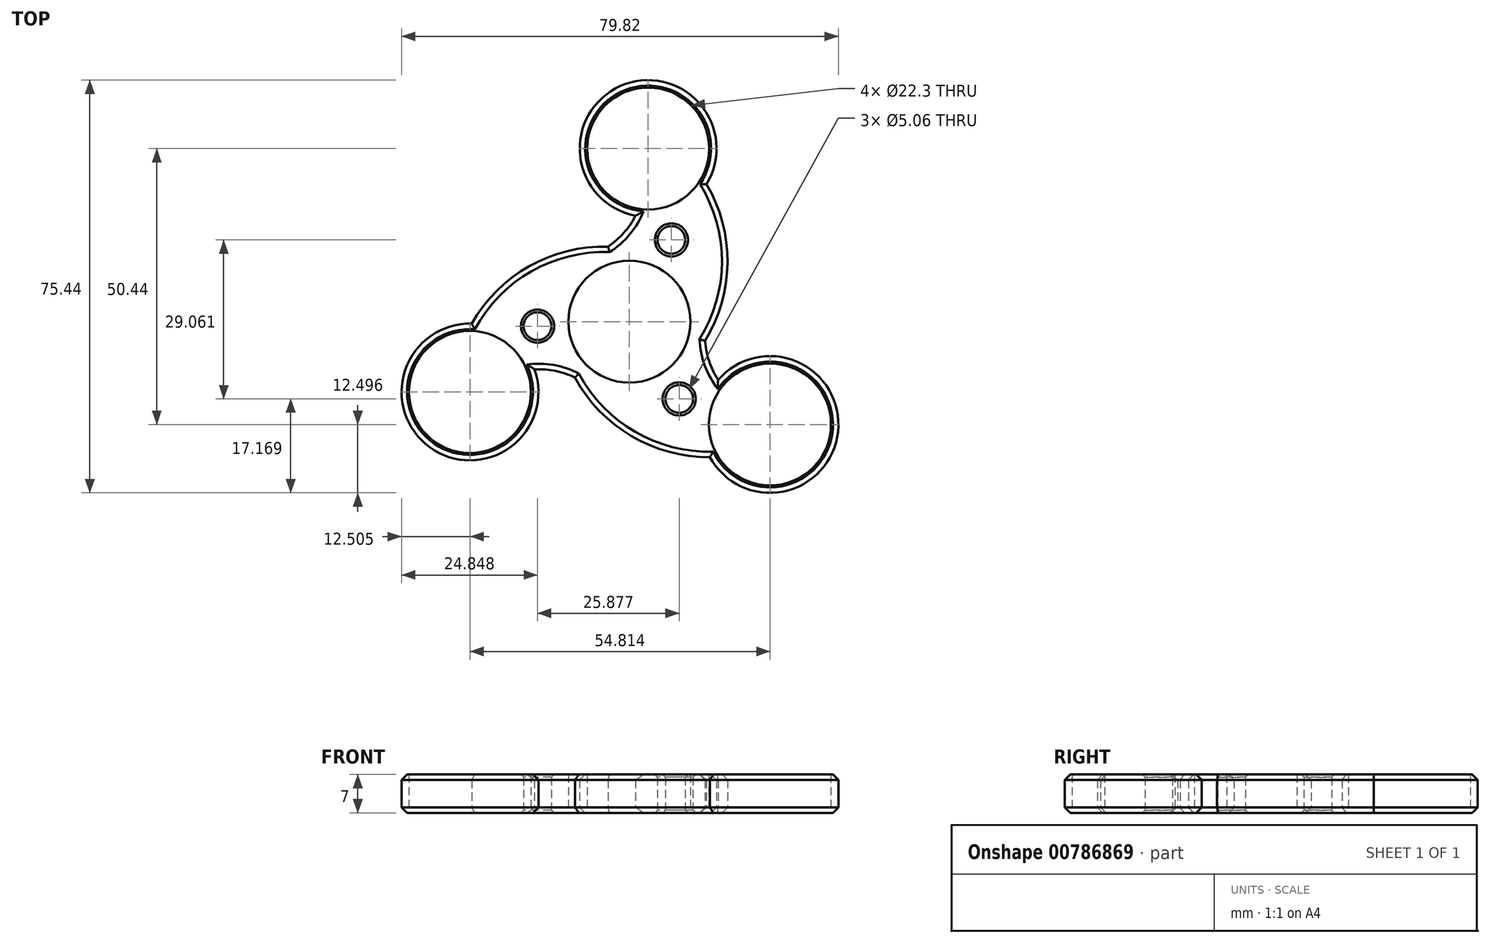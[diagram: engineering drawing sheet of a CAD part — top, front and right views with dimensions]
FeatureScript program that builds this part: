
annotation { "Feature Type Name" : "Feature", "Feature Type Description" : "" }
export const myFeature = defineFeature(function(context is Context, id is Id, definition is map)
    precondition{}
    {
        {
            var Q0;
            Q0=qCreatedBy(makeId("Top.planeOp"),FACE);
            var sketch = newSketch(context, id + "F0", { "sketchPlane" : qUnion([Q0])});
            skCircle(sketch, "E0", {"center": v(-20.85, 25.1) * mm, "radius": 11.15 * mm});
            skArc(sketch, "E1", {"start": v(-30.79, 14.88) * mm, "mid": v(-20.48, 4.2) * mm, "end": v(-6.14, 0.34) * mm});
            skArc(sketch, "E2", {"start": v(-7.03, 21.62) * mm, "mid": v(-6.3, 17.89) * mm, "end": v(-4.64, 14.46) * mm});
            skCircle(sketch, "E3", {"center": v(4.84, 6.32) * mm, "radius": 11.15 * mm});
            skArc(sketch, "E4", {"start": v(-6.14, 0.34) * mm, "mid": v(17.27, 5) * mm, "end": v(-4.64, 14.46) * mm});
            skArc(sketch, "E5.1.0", {"start": v(-24.74, 38.83) * mm, "mid": v(-21.88, 41.33) * mm, "end": v(-19.74, 44.47) * mm});
            skCircle(sketch, "E5.1.1", {"center": v(-17.42, 56.76) * mm, "radius": 11.15 * mm});
            skArc(sketch, "E5.1.2", {"start": v(-6.76, 50.24) * mm, "mid": v(-22.5, 68.18) * mm, "end": v(-19.74, 44.47) * mm});
            skArc(sketch, "E5.1.3", {"start": v(-7.03, 21.62) * mm, "mid": v(-2.94, 35.9) * mm, "end": v(-6.76, 50.24) * mm});
            skArc(sketch, "E5.2.0", {"start": v(-30.79, 14.88) * mm, "mid": v(-34.39, 16.11) * mm, "end": v(-38.18, 16.4) * mm});
            skCircle(sketch, "E5.2.1", {"center": v(-49.98, 12.26) * mm, "radius": 11.15 * mm});
            skArc(sketch, "E5.2.2", {"start": v(-49.66, 24.75) * mm, "mid": v(-57.33, 2.15) * mm, "end": v(-38.18, 16.4) * mm});
            skArc(sketch, "E5.2.3", {"start": v(-24.74, 38.83) * mm, "mid": v(-39.15, 35.24) * mm, "end": v(-49.66, 24.75) * mm});
            skPoint(sketch, "E6.trimOffspring.end.orphan", {"position": v(-6.85, 25.1) * mm});
            skPoint(sketch, "E7.orphan", {"position": v(-7.52, 20.85) * mm});
            skPoint(sketch, "E8.orphan", {"position": v(-27.85, 12.99) * mm});
            skPoint(sketch, "E9.orphan", {"position": v(-31.21, 15.7) * mm});
            skPoint(sketch, "E10.orphan", {"position": v(-27.85, 37.23) * mm});
            skPoint(sketch, "E11.orphan", {"position": v(-23.83, 38.79) * mm});
            skCircle(sketch, "E12", {"center": v(-13.17, 40.05) * mm, "radius": 2.53 * mm});
            skCircle(sketch, "E13.1.0", {"center": v(-37.63, 24.3) * mm, "radius": 2.53 * mm});
            skCircle(sketch, "E13.2.0", {"center": v(-11.75, 10.99) * mm, "radius": 2.53 * mm});
            skSolve(sketch);
        }
        {
            var Q0;
            Q0=qSketchRegion(id+"F0",true);
            extrude(context, id + "F1", {"entities" : qUnion([Q0]), "depth" : 7 * mm, "offsetDistance" : 25 * mm});
        }
        {
            var Q0;
            Q0=makeQuery(id+"F1.opExtrude","CAP_EDGE",EDGE,{"disambiguationData":[OSD([sQuery(id+"F0.wireOp",EDGE,"E5.2.3")])],"isStart":true});
            var Q1;
            Q1=makeQuery(id+"F1.opExtrude","CAP_EDGE",EDGE,{"disambiguationData":[OSD([sQuery(id+"F0.wireOp",EDGE,"E5.2.3")])],"isStart":false});
            var Q2;
            Q2=makeQuery(id+"F1.opExtrude","CAP_EDGE",EDGE,{"disambiguationData":[OSD([sQuery(id+"F0.wireOp",EDGE,"E5.2.2")])],"isStart":true});
            var Q3;
            Q3=makeQuery(id+"F1.opExtrude","CAP_EDGE",EDGE,{"disambiguationData":[OSD([sQuery(id+"F0.wireOp",EDGE,"E5.2.2")])],"isStart":false});
            var Q4;
            Q4=makeQuery(id+"F1.opExtrude","CAP_EDGE",EDGE,{"disambiguationData":[OSD([sQuery(id+"F0.wireOp",EDGE,"E5.1.0")])],"isStart":false});
            var Q5;
            Q5=makeQuery(id+"F1.opExtrude","CAP_EDGE",EDGE,{"disambiguationData":[OSD([sQuery(id+"F0.wireOp",EDGE,"E5.1.0")])],"isStart":true});
            var Q6;
            Q6=makeQuery(id+"F1.opExtrude","CAP_EDGE",EDGE,{"disambiguationData":[OSD([sQuery(id+"F0.wireOp",EDGE,"E5.1.2")])],"isStart":true});
            var Q7;
            Q7=makeQuery(id+"F1.opExtrude","CAP_EDGE",EDGE,{"disambiguationData":[OSD([sQuery(id+"F0.wireOp",EDGE,"E5.1.2")])],"isStart":false});
            var Q8;
            Q8=makeQuery(id+"F1.opExtrude","CAP_EDGE",EDGE,{"disambiguationData":[OSD([sQuery(id+"F0.wireOp",EDGE,"E5.1.3")])],"isStart":true});
            var Q9;
            Q9=makeQuery(id+"F1.opExtrude","CAP_EDGE",EDGE,{"disambiguationData":[OSD([sQuery(id+"F0.wireOp",EDGE,"E5.1.3")])],"isStart":false});
            var Q10;
            Q10=makeQuery(id+"F1.opExtrude","CAP_EDGE",EDGE,{"disambiguationData":[OSD([sQuery(id+"F0.wireOp",EDGE,"E2")])],"isStart":false});
            var Q11;
            Q11=makeQuery(id+"F1.opExtrude","CAP_EDGE",EDGE,{"disambiguationData":[OSD([sQuery(id+"F0.wireOp",EDGE,"E2")])],"isStart":true});
            var Q12;
            Q12=makeQuery(id+"F1.opExtrude","CAP_EDGE",EDGE,{"disambiguationData":[OSD([sQuery(id+"F0.wireOp",EDGE,"E4")])],"isStart":true});
            var Q13;
            Q13=makeQuery(id+"F1.opExtrude","CAP_EDGE",EDGE,{"disambiguationData":[OSD([sQuery(id+"F0.wireOp",EDGE,"E4")])],"isStart":false});
            var Q14;
            Q14=makeQuery(id+"F1.opExtrude","CAP_EDGE",EDGE,{"disambiguationData":[OSD([sQuery(id+"F0.wireOp",EDGE,"E1")])],"isStart":true});
            var Q15;
            Q15=makeQuery(id+"F1.opExtrude","CAP_EDGE",EDGE,{"disambiguationData":[OSD([sQuery(id+"F0.wireOp",EDGE,"E1")])],"isStart":false});
            var Q16;
            Q16=makeQuery(id+"F1.opExtrude","CAP_EDGE",EDGE,{"disambiguationData":[OSD([sQuery(id+"F0.wireOp",EDGE,"E5.2.0")])],"isStart":false});
            var Q17;
            Q17=makeQuery(id+"F1.opExtrude","CAP_EDGE",EDGE,{"disambiguationData":[OSD([sQuery(id+"F0.wireOp",EDGE,"E5.2.0")])],"isStart":true});
            chamfer(context, id + "F2", {"entities" : qUnion([Q0, Q1, Q2, Q3, Q4, Q5, Q6, Q7, Q8, Q9, Q10, Q11, Q12, Q13, Q14, Q15, Q16, Q17]), "width" : 1 * mm, "tangentPropagation" : true});
        }
        {
            var Q0;
            Q0=makeQuery(id+"F1.opExtrude","CAP_EDGE",EDGE,{"disambiguationData":[OSD([sQuery(id+"F0.wireOp",EDGE,"E13.1.0")])],"isStart":false});
            var Q1;
            Q1=makeQuery(id+"F1.opExtrude","CAP_EDGE",EDGE,{"disambiguationData":[OSD([sQuery(id+"F0.wireOp",EDGE,"E12")])],"isStart":false});
            var Q2;
            Q2=makeQuery(id+"F1.opExtrude","CAP_EDGE",EDGE,{"disambiguationData":[OSD([sQuery(id+"F0.wireOp",EDGE,"E13.2.0")])],"isStart":false});
            var Q3;
            Q3=makeQuery(id+"F1.opExtrude","CAP_EDGE",EDGE,{"disambiguationData":[OSD([sQuery(id+"F0.wireOp",EDGE,"E13.1.0")])],"isStart":true});
            var Q4;
            Q4=makeQuery(id+"F1.opExtrude","CAP_EDGE",EDGE,{"disambiguationData":[OSD([sQuery(id+"F0.wireOp",EDGE,"E12")])],"isStart":true});
            var Q5;
            Q5=makeQuery(id+"F1.opExtrude","CAP_EDGE",EDGE,{"disambiguationData":[OSD([sQuery(id+"F0.wireOp",EDGE,"E13.2.0")])],"isStart":true});
            chamfer(context, id + "F3", {"entities" : qUnion([Q0, Q1, Q2, Q3, Q4, Q5]), "width" : 0.5 * mm, "tangentPropagation" : true});
        }
    });
